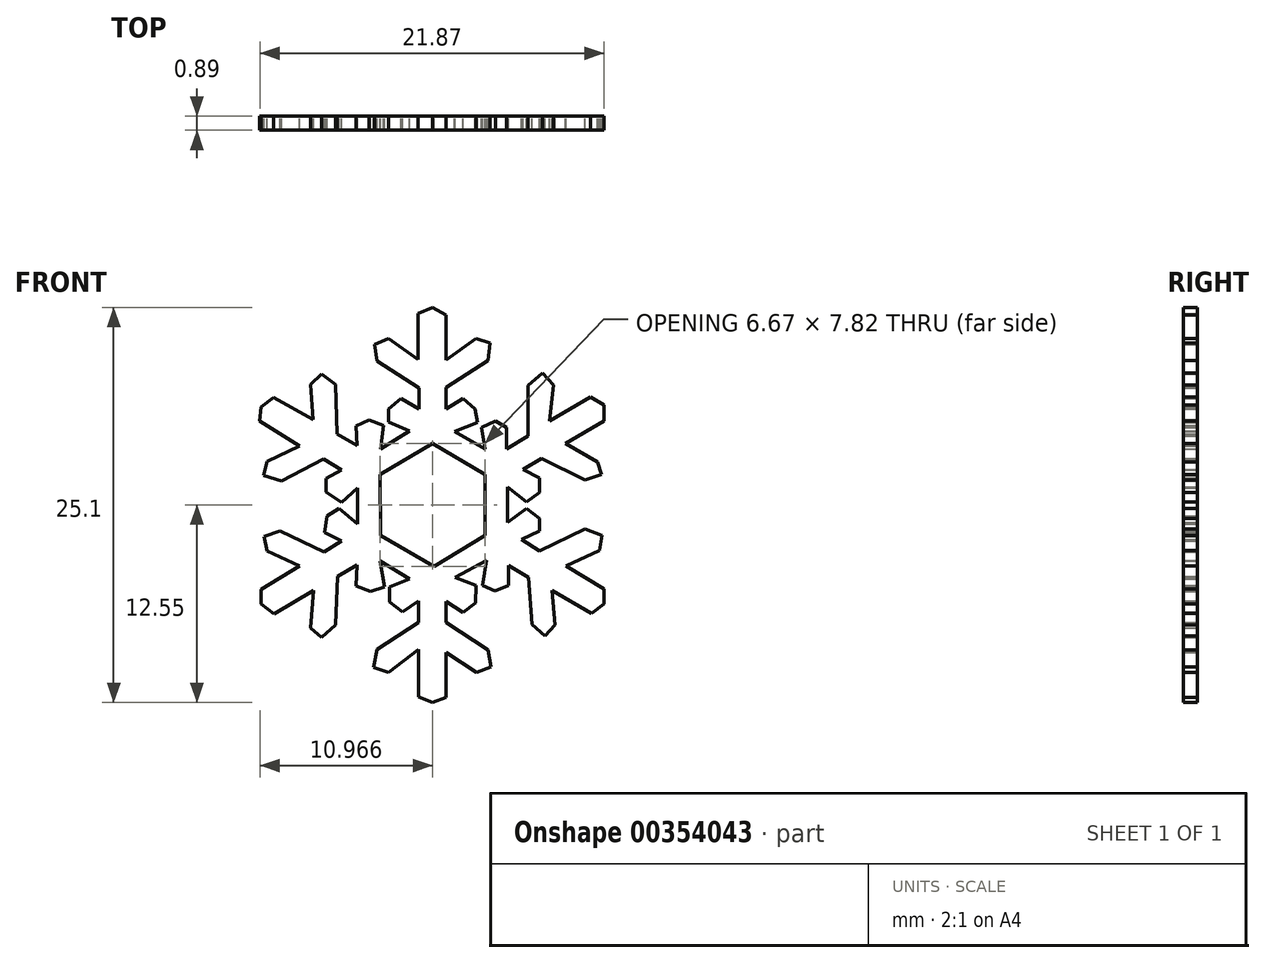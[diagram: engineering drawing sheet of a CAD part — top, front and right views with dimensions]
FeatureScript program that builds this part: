
annotation { "Feature Type Name" : "Feature", "Feature Type Description" : "" }
export const myFeature = defineFeature(function(context is Context, id is Id, definition is map)
    precondition{}
    {
        {
            var Q0;
            Q0=qCreatedBy(makeId("Front.planeOp"),FACE);
            var sketch = newSketch(context, id + "F0", { "sketchPlane" : qUnion([Q0])});
            skLineSegment(sketch, "E0", {"start": v(-14.44, 0.41) * mm, "end": v(-11.12, 2.4) * mm});
            skLineSegment(sketch, "E1", {"start": v(-11.12, 2.4) * mm, "end": v(-7.77, 0.44) * mm});
            skLineSegment(sketch, "E2", {"start": v(-7.77, 0.44) * mm, "end": v(-7.77, -3.45) * mm});
            skLineSegment(sketch, "E3", {"start": v(-7.77, -3.45) * mm, "end": v(-11.02, -5.43) * mm});
            skLineSegment(sketch, "E4", {"start": v(-11.02, -5.43) * mm, "end": v(-14.42, -3.45) * mm});
            skLineSegment(sketch, "E5", {"start": v(-14.42, -3.45) * mm, "end": v(-14.44, 0.41) * mm});
            skLineSegment(sketch, "E6", {"start": v(-9.7, 3.15) * mm, "end": v(-7.77, 2.05) * mm});
            skLineSegment(sketch, "E7", {"start": v(-7.77, 2.05) * mm, "end": v(-7.99, 3.42) * mm});
            skLineSegment(sketch, "E8", {"start": v(-7.99, 3.42) * mm, "end": v(-7.1, 3.8) * mm});
            skLineSegment(sketch, "E9", {"start": v(-7.1, 3.8) * mm, "end": v(-6.42, 3.42) * mm});
            skLineSegment(sketch, "E10", {"start": v(-6.42, 3.42) * mm, "end": v(-6.42, 2.05) * mm});
            skLineSegment(sketch, "E11", {"start": v(-6.42, 2.05) * mm, "end": v(-5.03, 2.86) * mm});
            skLineSegment(sketch, "E12", {"start": v(-5.03, 2.86) * mm, "end": v(-5.03, 6.06) * mm});
            skLineSegment(sketch, "E13", {"start": v(-5.03, 6.06) * mm, "end": v(-4.12, 6.87) * mm});
            skLineSegment(sketch, "E14", {"start": v(-4.12, 6.87) * mm, "end": v(-3.42, 6.1) * mm});
            skLineSegment(sketch, "E15", {"start": v(-3.42, 6.1) * mm, "end": v(-3.68, 3.8) * mm});
            skLineSegment(sketch, "E16", {"start": v(-3.68, 3.8) * mm, "end": v(-1.07, 5.33) * mm});
            skLineSegment(sketch, "E17", {"start": v(-1.07, 5.33) * mm, "end": v(-0.23, 4.85) * mm});
            skLineSegment(sketch, "E18", {"start": v(-0.23, 4.85) * mm, "end": v(-0.23, 3.8) * mm});
            skLineSegment(sketch, "E19", {"start": v(-0.23, 3.8) * mm, "end": v(-2.67, 2.4) * mm});
            skLineSegment(sketch, "E20", {"start": v(-2.67, 2.4) * mm, "end": v(-0.62, 1.22) * mm});
            skLineSegment(sketch, "E21", {"start": v(-0.62, 1.22) * mm, "end": v(-0.37, 0.41) * mm});
            skLineSegment(sketch, "E22", {"start": v(-0.37, 0.41) * mm, "end": v(-1.43, 0.08) * mm});
            skLineSegment(sketch, "E23", {"start": v(-1.43, 0.08) * mm, "end": v(-4.18, 1.45) * mm});
            skLineSegment(sketch, "E24", {"start": v(-4.18, 1.45) * mm, "end": v(-5.35, 0.74) * mm});
            skLineSegment(sketch, "E25", {"start": v(-5.35, 0.74) * mm, "end": v(-4.3, 0.2) * mm});
            skLineSegment(sketch, "E26", {"start": v(-4.3, 0.2) * mm, "end": v(-4.3, -0.73) * mm});
            skLineSegment(sketch, "E27", {"start": v(-4.3, -0.73) * mm, "end": v(-5.13, -1.31) * mm});
            skLineSegment(sketch, "E28", {"start": v(-5.13, -1.31) * mm, "end": v(-6.34, -0.39) * mm});
            skLineSegment(sketch, "E29", {"start": v(-6.34, -0.39) * mm, "end": v(-6.34, -2.61) * mm});
            skLineSegment(sketch, "E30", {"start": v(-6.34, -2.61) * mm, "end": v(-5.13, -1.75) * mm});
            skLineSegment(sketch, "E31", {"start": v(-5.13, -1.75) * mm, "end": v(-4.3, -2.37) * mm});
            skLineSegment(sketch, "E32", {"start": v(-4.3, -2.37) * mm, "end": v(-4.3, -3.18) * mm});
            skLineSegment(sketch, "E33", {"start": v(-4.3, -3.18) * mm, "end": v(-5.44, -3.71) * mm});
            skLineSegment(sketch, "E34", {"start": v(-5.44, -3.71) * mm, "end": v(-4.3, -4.45) * mm});
            skLineSegment(sketch, "E35", {"start": v(-4.3, -4.45) * mm, "end": v(-1.43, -3.03) * mm});
            skLineSegment(sketch, "E36", {"start": v(-1.43, -3.03) * mm, "end": v(-0.36, -3.44) * mm});
            skLineSegment(sketch, "E37", {"start": v(-0.36, -3.44) * mm, "end": v(-0.5, -4.4) * mm});
            skLineSegment(sketch, "E38", {"start": v(-0.5, -4.4) * mm, "end": v(-2.62, -5.4) * mm});
            skLineSegment(sketch, "E39", {"start": v(-2.62, -5.4) * mm, "end": v(-0.2, -6.86) * mm});
            skLineSegment(sketch, "E40", {"start": v(-0.2, -6.86) * mm, "end": v(-0.2, -7.81) * mm});
            skLineSegment(sketch, "E41", {"start": v(-0.2, -7.81) * mm, "end": v(-1.02, -8.4) * mm});
            skLineSegment(sketch, "E42", {"start": v(-1.02, -8.4) * mm, "end": v(-3.5, -6.93) * mm});
            skLineSegment(sketch, "E43", {"start": v(-3.5, -6.93) * mm, "end": v(-3.33, -9.13) * mm});
            skLineSegment(sketch, "E44", {"start": v(-3.33, -9.13) * mm, "end": v(-3.97, -9.84) * mm});
            skLineSegment(sketch, "E45", {"start": v(-3.97, -9.84) * mm, "end": v(-4.8, -9.1) * mm});
            skLineSegment(sketch, "E46", {"start": v(-4.8, -9.1) * mm, "end": v(-5, -6.13) * mm});
            skLineSegment(sketch, "E47", {"start": v(-5, -6.13) * mm, "end": v(-6.3, -5.34) * mm});
            skLineSegment(sketch, "E48", {"start": v(-6.3, -5.34) * mm, "end": v(-6.3, -6.64) * mm});
            skLineSegment(sketch, "E49", {"start": v(-6.3, -6.64) * mm, "end": v(-7.12, -6.98) * mm});
            skLineSegment(sketch, "E50", {"start": v(-7.12, -6.98) * mm, "end": v(-7.93, -6.64) * mm});
            skLineSegment(sketch, "E51", {"start": v(-7.93, -6.64) * mm, "end": v(-7.66, -5.05) * mm});
            skLineSegment(sketch, "E52", {"start": v(-7.66, -5.05) * mm, "end": v(-9.7, -6.13) * mm});
            skLineSegment(sketch, "E53", {"start": v(-9.7, -6.13) * mm, "end": v(-8.35, -6.64) * mm});
            skLineSegment(sketch, "E54", {"start": v(-8.37, -7.74) * mm, "end": v(-9.18, -8.35) * mm});
            skLineSegment(sketch, "E55", {"start": v(-9.18, -8.35) * mm, "end": v(-10.25, -7.64) * mm});
            skLineSegment(sketch, "E56", {"start": v(-10.25, -7.64) * mm, "end": v(-10.25, -8.96) * mm});
            skLineSegment(sketch, "E57", {"start": v(-10.25, -8.96) * mm, "end": v(-7.58, -10.72) * mm});
            skLineSegment(sketch, "E58", {"start": v(-7.58, -10.72) * mm, "end": v(-7.4, -11.8) * mm});
            skLineSegment(sketch, "E59", {"start": v(-7.4, -11.8) * mm, "end": v(-8.32, -12.15) * mm});
            skLineSegment(sketch, "E60", {"start": v(-8.32, -12.15) * mm, "end": v(-10.25, -10.88) * mm});
            skLineSegment(sketch, "E61", {"start": v(-10.25, -13.74) * mm, "end": v(-11.11, -14.07) * mm});
            skPoint(sketch, "E61.endSnap0", {"position": v(-11.11, -14.24) * mm});
            skLineSegment(sketch, "E62", {"start": v(-11.11, -14.07) * mm, "end": v(-11.98, -13.7) * mm});
            skLineSegment(sketch, "E63", {"start": v(-10.25, -13.74) * mm, "end": v(-10.25, -10.88) * mm});
            skLineSegment(sketch, "E64", {"start": v(-11.98, -13.7) * mm, "end": v(-11.98, -10.7) * mm});
            skLineSegment(sketch, "E65", {"start": v(-11.98, -10.7) * mm, "end": v(-13.9, -12.16) * mm});
            skLineSegment(sketch, "E66", {"start": v(-13.9, -12.16) * mm, "end": v(-14.85, -11.83) * mm});
            skLineSegment(sketch, "E67", {"start": v(-14.85, -11.83) * mm, "end": v(-14.62, -10.7) * mm});
            skLineSegment(sketch, "E68", {"start": v(-14.62, -10.7) * mm, "end": v(-11.99, -8.98) * mm});
            skLineSegment(sketch, "E69", {"start": v(-11.99, -8.98) * mm, "end": v(-11.99, -7.6) * mm});
            skLineSegment(sketch, "E70", {"start": v(-11.99, -7.6) * mm, "end": v(-13.02, -8.32) * mm});
            skLineSegment(sketch, "E71", {"start": v(-13.02, -8.32) * mm, "end": v(-13.83, -7.66) * mm});
            skLineSegment(sketch, "E72", {"start": v(-13.83, -7.66) * mm, "end": v(-13.83, -6.72) * mm});
            skLineSegment(sketch, "E73", {"start": v(-13.83, -6.72) * mm, "end": v(-12.57, -6.2) * mm});
            skLineSegment(sketch, "E74", {"start": v(-12.57, -6.2) * mm, "end": v(-14.44, -5.06) * mm});
            skLineSegment(sketch, "E75", {"start": v(-14.44, -5.06) * mm, "end": v(-14.16, -6.72) * mm});
            skLineSegment(sketch, "E76", {"start": v(-14.16, -6.72) * mm, "end": v(-15.03, -7) * mm});
            skLineSegment(sketch, "E77", {"start": v(-15.03, -7) * mm, "end": v(-15.95, -6.66) * mm});
            skLineSegment(sketch, "E78", {"start": v(-15.95, -6.66) * mm, "end": v(-15.9, -5.32) * mm});
            skLineSegment(sketch, "E79", {"start": v(-15.9, -5.32) * mm, "end": v(-17.14, -6.06) * mm});
            skLineSegment(sketch, "E80", {"start": v(-17.14, -6.06) * mm, "end": v(-17.28, -9.15) * mm});
            skLineSegment(sketch, "E81", {"start": v(-17.28, -9.15) * mm, "end": v(-18.17, -9.94) * mm});
            skLineSegment(sketch, "E82", {"start": v(-18.17, -9.94) * mm, "end": v(-18.85, -9.34) * mm});
            skLineSegment(sketch, "E83", {"start": v(-18.85, -9.34) * mm, "end": v(-18.65, -6.95) * mm});
            skLineSegment(sketch, "E84", {"start": v(-18.65, -6.95) * mm, "end": v(-21.17, -8.45) * mm});
            skLineSegment(sketch, "E85", {"start": v(-21.17, -8.45) * mm, "end": v(-22, -7.8) * mm});
            skLineSegment(sketch, "E86", {"start": v(-22, -7.8) * mm, "end": v(-22, -6.89) * mm});
            skLineSegment(sketch, "E87", {"start": v(-22, -6.89) * mm, "end": v(-19.56, -5.4) * mm});
            skLineSegment(sketch, "E88", {"start": v(-19.56, -5.4) * mm, "end": v(-21.6, -4.43) * mm});
            skLineSegment(sketch, "E89", {"start": v(-21.6, -4.43) * mm, "end": v(-21.8, -3.52) * mm});
            skLineSegment(sketch, "E90", {"start": v(-21.8, -3.52) * mm, "end": v(-20.78, -3.15) * mm});
            skLineSegment(sketch, "E91", {"start": v(-20.78, -3.15) * mm, "end": v(-18, -4.49) * mm});
            skLineSegment(sketch, "E92", {"start": v(-18, -4.49) * mm, "end": v(-16.88, -3.8) * mm});
            skLineSegment(sketch, "E93", {"start": v(-16.88, -3.8) * mm, "end": v(-17.96, -3.27) * mm});
            skLineSegment(sketch, "E94", {"start": v(-17.96, -3.27) * mm, "end": v(-17.81, -2.22) * mm});
            skLineSegment(sketch, "E95", {"start": v(-17.81, -2.22) * mm, "end": v(-17.04, -1.75) * mm});
            skLineSegment(sketch, "E96", {"start": v(-17.04, -1.75) * mm, "end": v(-15.86, -2.72) * mm});
            skLineSegment(sketch, "E97", {"start": v(-15.86, -2.72) * mm, "end": v(-15.86, -0.44) * mm});
            skLineSegment(sketch, "E98", {"start": v(-15.86, -0.44) * mm, "end": v(-16.89, -1.36) * mm});
            skLineSegment(sketch, "E99", {"start": v(-16.89, -1.36) * mm, "end": v(-17.85, -0.68) * mm});
            skLineSegment(sketch, "E100", {"start": v(-17.85, -0.68) * mm, "end": v(-17.85, 0.18) * mm});
            skLineSegment(sketch, "E101", {"start": v(-17.85, 0.18) * mm, "end": v(-16.87, 0.7) * mm});
            skLineSegment(sketch, "E102", {"start": v(-16.87, 0.7) * mm, "end": v(-18.02, 1.4) * mm});
            skLineSegment(sketch, "E103", {"start": v(-18.02, 1.4) * mm, "end": v(-20.7, 0) * mm});
            skLineSegment(sketch, "E104", {"start": v(-20.7, 0) * mm, "end": v(-21.88, 0.38) * mm});
            skLineSegment(sketch, "E105", {"start": v(-21.85, 0.35) * mm, "end": v(-21.62, 1.25) * mm});
            skLineSegment(sketch, "E106", {"start": v(-21.62, 1.25) * mm, "end": v(-19.56, 2.24) * mm});
            skLineSegment(sketch, "E107", {"start": v(-19.56, 2.24) * mm, "end": v(-22.07, 3.8) * mm});
            skLineSegment(sketch, "E108", {"start": v(-22.07, 3.8) * mm, "end": v(-22, 4.7) * mm});
            skLineSegment(sketch, "E109", {"start": v(-22, 4.7) * mm, "end": v(-21.21, 5.32) * mm});
            skLineSegment(sketch, "E110", {"start": v(-21.21, 5.32) * mm, "end": v(-18.68, 3.91) * mm});
            skLineSegment(sketch, "E111", {"start": v(-18.68, 3.91) * mm, "end": v(-18.85, 6.14) * mm});
            skLineSegment(sketch, "E112", {"start": v(-18.85, 6.14) * mm, "end": v(-18.17, 6.8) * mm});
            skLineSegment(sketch, "E113", {"start": v(-18.17, 6.8) * mm, "end": v(-17.27, 6.14) * mm});
            skLineSegment(sketch, "E114", {"start": v(-17.27, 6.14) * mm, "end": v(-17.15, 2.99) * mm});
            skLineSegment(sketch, "E115", {"start": v(-17.15, 2.99) * mm, "end": v(-15.9, 2.27) * mm});
            skLineSegment(sketch, "E116", {"start": v(-15.9, 2.27) * mm, "end": v(-15.95, 3.51) * mm});
            skLineSegment(sketch, "E117", {"start": v(-15.95, 3.51) * mm, "end": v(-15.12, 3.87) * mm});
            skLineSegment(sketch, "E118", {"start": v(-15.12, 3.87) * mm, "end": v(-14.22, 3.54) * mm});
            skLineSegment(sketch, "E119", {"start": v(-14.22, 3.54) * mm, "end": v(-14.42, 2.04) * mm});
            skLineSegment(sketch, "E120", {"start": v(-14.42, 2.04) * mm, "end": v(-12.57, 3.17) * mm});
            skLineSegment(sketch, "E121", {"start": v(-12.57, 3.17) * mm, "end": v(-13.9, 3.74) * mm});
            skLineSegment(sketch, "E122", {"start": v(-13.9, 3.74) * mm, "end": v(-13.9, 4.59) * mm});
            skLineSegment(sketch, "E123", {"start": v(-13.9, 4.59) * mm, "end": v(-13.1, 5.23) * mm});
            skLineSegment(sketch, "E124", {"start": v(-13.1, 5.23) * mm, "end": v(-11.97, 4.59) * mm});
            skLineSegment(sketch, "E125", {"start": v(-11.97, 4.59) * mm, "end": v(-11.97, 5.9) * mm});
            skLineSegment(sketch, "E126", {"start": v(-11.97, 5.9) * mm, "end": v(-14.62, 7.61) * mm});
            skLineSegment(sketch, "E127", {"start": v(-14.62, 7.61) * mm, "end": v(-14.8, 8.68) * mm});
            skLineSegment(sketch, "E128", {"start": v(-14.8, 8.68) * mm, "end": v(-13.9, 9.05) * mm});
            skLineSegment(sketch, "E129", {"start": v(-13.9, 9.05) * mm, "end": v(-12.03, 7.74) * mm});
            skLineSegment(sketch, "E130", {"start": v(-12.03, 7.74) * mm, "end": v(-12.03, 10.66) * mm});
            skLineSegment(sketch, "E131", {"start": v(-12.03, 10.66) * mm, "end": v(-11.11, 11.03) * mm});
            skPoint(sketch, "E131.endSnap0", {"position": v(-11.11, 11.16) * mm});
            skLineSegment(sketch, "E132", {"start": v(-11.11, 11.03) * mm, "end": v(-10.24, 10.55) * mm});
            skLineSegment(sketch, "E133", {"start": v(-10.24, 10.55) * mm, "end": v(-10.24, 7.7) * mm});
            skLineSegment(sketch, "E134", {"start": v(-10.24, 7.7) * mm, "end": v(-8.35, 9.05) * mm});
            skLineSegment(sketch, "E135", {"start": v(-8.35, 9.05) * mm, "end": v(-7.44, 8.77) * mm});
            skLineSegment(sketch, "E136", {"start": v(-7.44, 8.77) * mm, "end": v(-7.57, 7.64) * mm});
            skLineSegment(sketch, "E137", {"start": v(-7.57, 7.64) * mm, "end": v(-10.24, 5.94) * mm});
            skLineSegment(sketch, "E138", {"start": v(-10.24, 5.94) * mm, "end": v(-10.24, 4.59) * mm});
            skLineSegment(sketch, "E139", {"start": v(-10.24, 4.59) * mm, "end": v(-9.17, 5.24) * mm});
            skLineSegment(sketch, "E140", {"start": v(-9.17, 5.24) * mm, "end": v(-8.4, 4.59) * mm});
            skLineSegment(sketch, "E141", {"start": v(-8.4, 4.59) * mm, "end": v(-8.25, 3.72) * mm});
            skLineSegment(sketch, "E142", {"start": v(-8.25, 3.72) * mm, "end": v(-9.7, 3.15) * mm});
            skLineSegment(sketch, "E143", {"start": v(-8.35, -6.64) * mm, "end": v(-8.37, -7.74) * mm});
            skSolve(sketch);
        }
        {
            var Q0;
            Q0=makeQuery(id+"F0.imprint","IMPRINT",FACE,{"disambiguationData":[TD([[makeQuery(id+"F0.imprint","IMPRINT",EDGE,{"derivedFrom":sQuery(id+"F0.wireOp",EDGE,"E0")}),1.0]])]});
            extrude(context, id + "F1", {"entities" : qUnion([Q0]), "depth" : 0.89 * mm});
        }
    });
